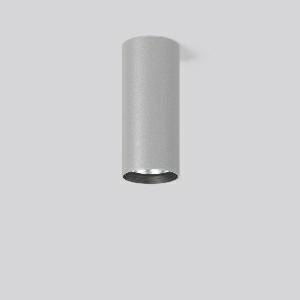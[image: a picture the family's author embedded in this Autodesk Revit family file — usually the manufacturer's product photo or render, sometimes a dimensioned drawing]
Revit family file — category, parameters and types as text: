
# Revit family: heledon_mini_a_931210_004_4664
name_source: partatom
category: Lighting Fixtures
units: mm (PartAtom-declared; Revit-internal decimal feet)

## family parameters
Cut with Voids When Loaded = No
Host = Face
Light Source = No
Part Type = Normal
Room Calculation Point = No
Round Connector Dimension = Use Diameter
Shared = No

## types (1)
- HELEDON mini A (1 x LED Modul 930, 3650 lm, 3000)
    Apparent Load = 29 VA
    Approval mark = CE
    CIE Flux Codes = 95 99 100 100 100
    Color Rendering = 90
    Color Temperature = 3000
    Default Elevation = 1800 mm
    Description = Series: HELEDON mini
Cylindrical surface-mounted downlight. Housing: die-cast aluminium, powder-coated. Internal ceiling frame polycarbonate with bayonet mounting. Black plastic ring and recessed LED to prevent glare from the side. Optical assembly with reflector made of MIRO-Silver with 98% total light reflection for outstanding efficiency - can be changed without tools. Best colour rendering index Ra>90. Suitable for Ceiling mounting. Easy installation with a separate ceiling frame with bayonet mounting and plug connection. Driver integrated. Connected via plug-in connector. High quality converter without flickering and stroboscopic effect. The following accessories can be mounted without use of tools: interchangeable lenses, decorative glasses, honeycomb louvre, clear and frosted diffusers, white interchangeable plastic ring. 
Colour: silver
Diameter: 87 mm
Height: 197 mm
Lamp: LED
Socket: without socket
Colour temperature: 3000K
Colour rendering index (CRI): 92
System power: 29 W
Rated luminous flux: 3650 lm
Luminous efficiency: 126 lm/W
Control gear: Regulated power supply
Protection class: I
Type of protection: IP 20
    Height = 197 mm
    Lamp = 1 x LED Modul 930
    Lamp Light Flux = 3650 lm
    Lamp count = 1
    Length = 87 mm
    Lifetime = 50000 h
    Luminous efficacy = 126 lm/W
    Manufacturer = RZB
    ModVariant = No
    Model = 931210.004
    Mounting Place = Ceiling
    Mounting Type = Surface mounted
    Number of Poles = 1
    OnlyDefault = Yes
    Power Factor = 1
    Product Name = HELEDON mini A
    Product group = Surface mounted downlights
    ProductGroupID = 302
    Protection Class = Protection class I
    Protection Degree = IP 20
    RLX_Detail_Level = 1
    RLX_Emergency_Light_Flux = 0 lm
    RLX_Emergency_Type = 0
    RLX_Emergency_Type_DB = No
    RlxData = <blob elided: 107709 chars, md5=0b0242af>
    Socket = socket
    Standby Power = 0 W
    System Light Flux = 3650 lm
    System Power = 29 W
    Type Comments = Product without accessories
    Type Image = 931188.004.jpg
    URL = http://relux.com
    VarID = ---
    Voltage = 230 V
    Voltage Range = 220-240 V
    Weight = 0.00 kg
    Width = 0 mm  [stored 0 ft]

note: [stored X ft] marks values corroborated as IEEE doubles in the binary element streams (Revit-internal decimal feet)

## geometry (parser evidence)
native form markers: Blend x4, Sweep x9
no freeform markers — native parametric forms only
